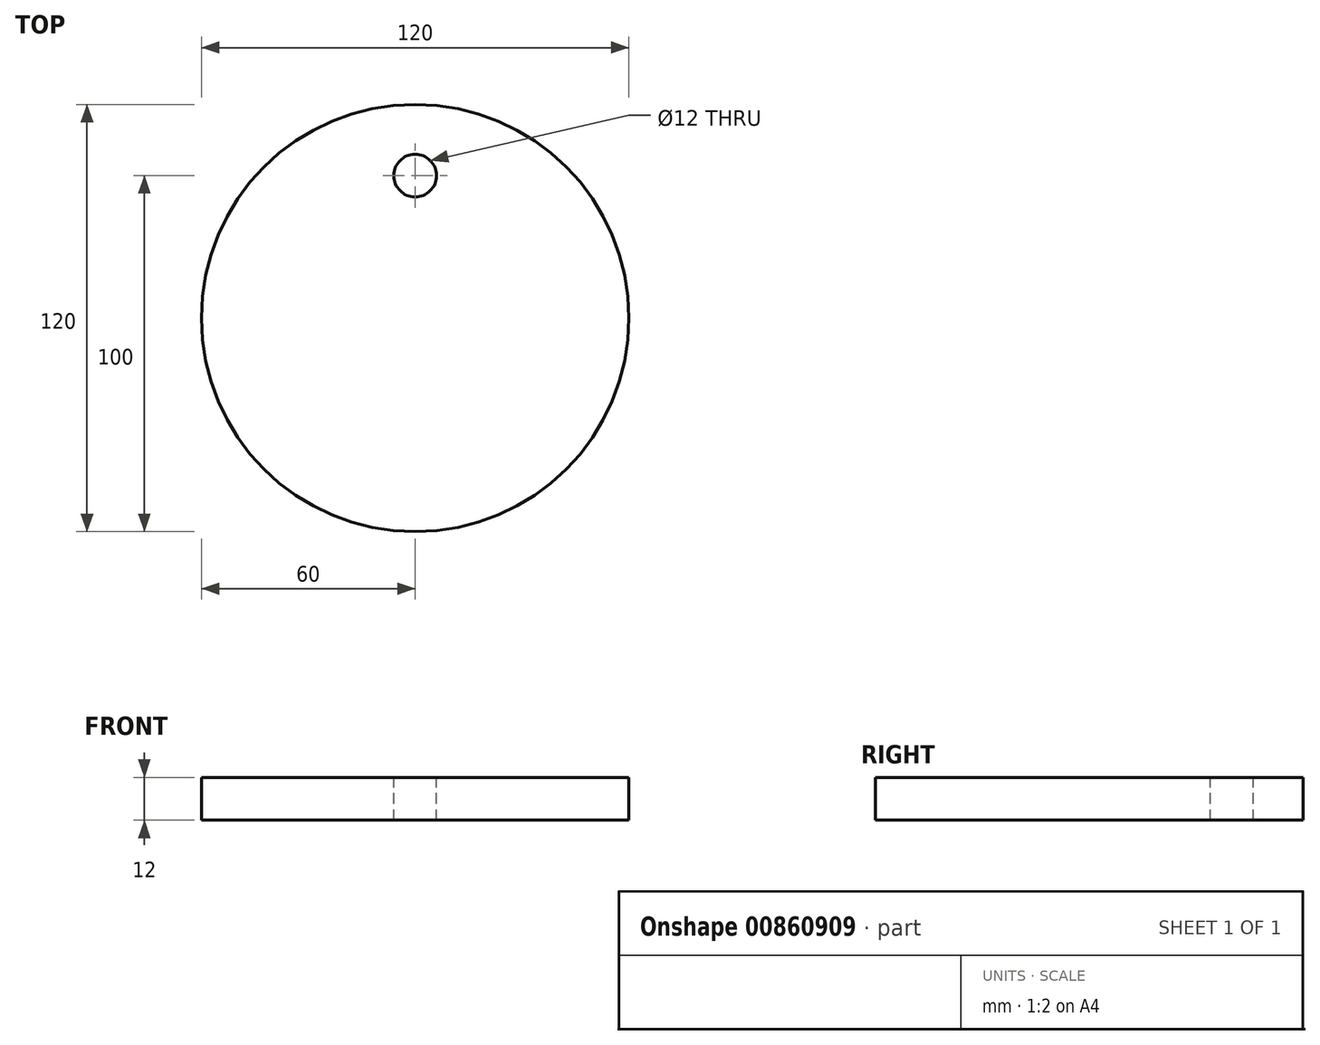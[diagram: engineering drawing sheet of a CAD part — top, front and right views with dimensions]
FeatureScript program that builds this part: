
annotation { "Feature Type Name" : "Feature", "Feature Type Description" : "" }
export const myFeature = defineFeature(function(context is Context, id is Id, definition is map)
    precondition{}
    {
        {
            assignVariable(context, id + "F0", {"name" : "big_circle", "anyValue" : 120});
        }
        {
            assignVariable(context, id + "F1", {"name" : "thickness", "anyValue" : getVariable(context, 'big_circle') / 10});
        }
        {
            var Q0;
            Q0=qCreatedBy(makeId("Top.planeOp"),FACE);
            var sketch = newSketch(context, id + "F2", { "sketchPlane" : qUnion([Q0])});
            skCircle(sketch, "E0", {"center": v(0, 0) * mm, "radius": 60 * mm});
            skSolve(sketch);
        }
        {
            var Q0;
            Q0 = qSketchRegion(id + "F2", true);
            extrude(context, id + "F3", {"entities" : qUnion([Q0]), "depth" : (getVariable(context, 'thickness')) * mm, "offsetDistance" : 25 * mm});
        }
        {
            var Q0;
            Q0=makeQuery(id+"F3.opExtrude","CAP_FACE",FACE,{"disambiguationData":[OSD([sQuery(id+"F2.wireOp",EDGE,"E0")])],"isStart":false});
            var sketch = newSketch(context, id + "F4", { "sketchPlane" : qUnion([Q0])});
            skCircle(sketch, "E1", {"center": v(0, 0) * mm, "radius": 40 * mm, "construction": true});
            skCircle(sketch, "E2", {"center": v(0, 40) * mm, "radius": 6 * mm});
            skSolve(sketch);
        }
        {
            var Q0;
            Q0=makeQuery(id+"F4.imprint","IMPRINT",FACE,{"disambiguationData":[TD([[makeQuery(id+"F4.imprint","IMPRINT",EDGE,{"derivedFrom":sQuery(id+"F4.wireOp",EDGE,"E2")}),1.0]])]});
            extrude(context, id + "F5", {"entities" : qUnion([Q0]), "operationType" : NewBodyOperationType.REMOVE, "endBound" : BoundingType.THROUGH_ALL, "oppositeDirection" : true, "depth" : 25 * mm, "offsetDistance" : 25 * mm});
        }
    });
